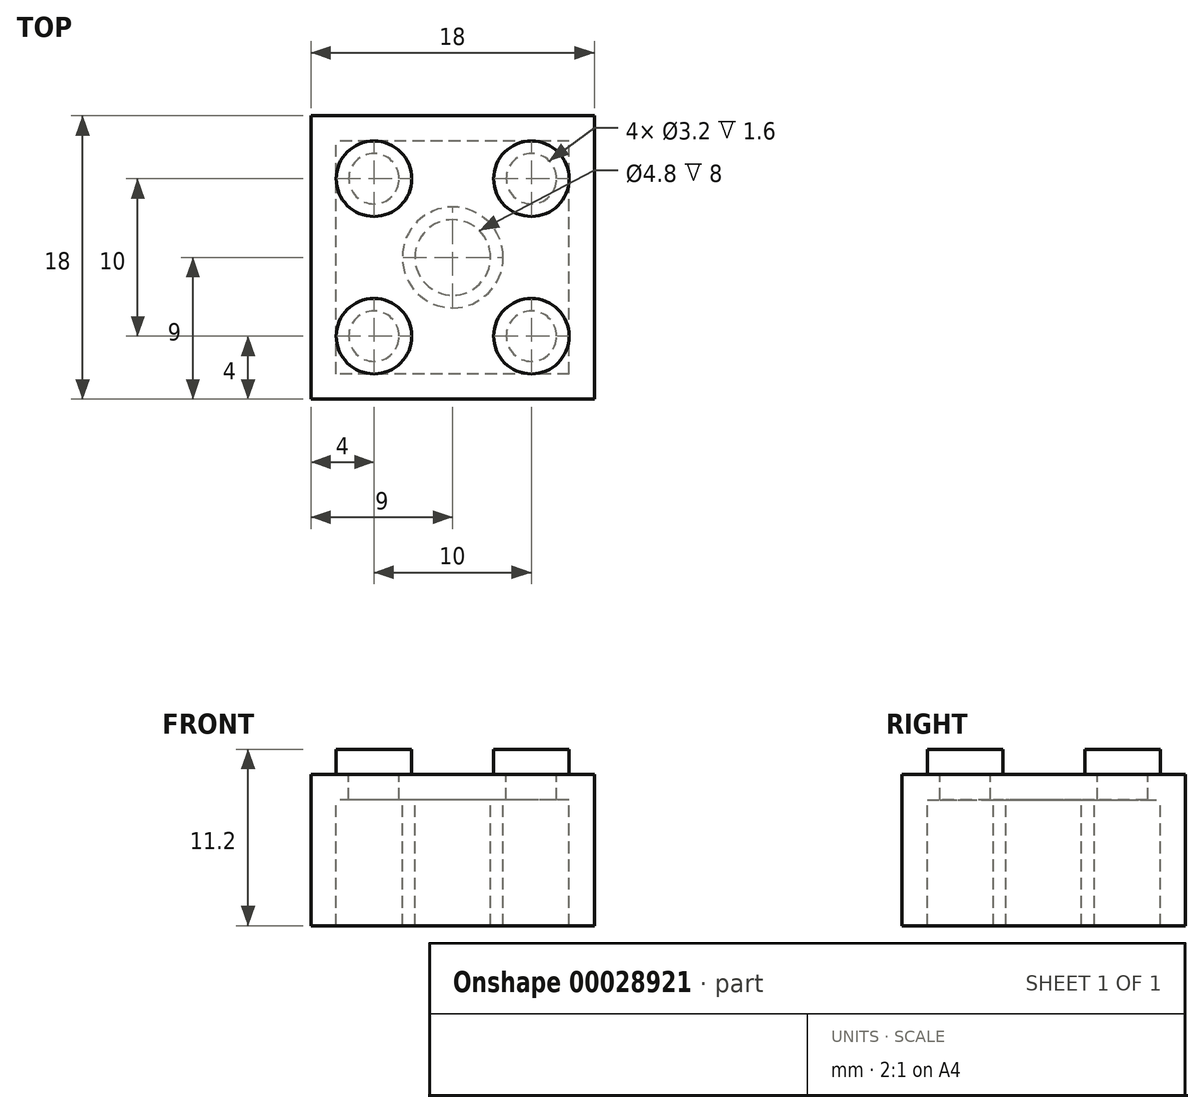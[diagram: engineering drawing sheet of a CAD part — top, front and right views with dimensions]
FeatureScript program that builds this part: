
annotation { "Feature Type Name" : "Feature", "Feature Type Description" : "" }
export const myFeature = defineFeature(function(context is Context, id is Id, definition is map)
    precondition{}
    {
        {
            var Q0;
            Q0=qCreatedBy(makeId("Top.planeOp"),FACE);
            var sketch = newSketch(context, id + "F0", { "sketchPlane" : qUnion([Q0])});
            skLineSegment(sketch, "E0.rect.bottom", {"start": v(9, -9) * mm, "end": v(-9, -9) * mm});
            skLineSegment(sketch, "E0.rect.top", {"start": v(9, 9) * mm, "end": v(-9, 9) * mm});
            skLineSegment(sketch, "E0.rect.left", {"start": v(9, -9) * mm, "end": v(9, 9) * mm});
            skLineSegment(sketch, "E0.rect.right", {"start": v(-9, -9) * mm, "end": v(-9, 9) * mm});
            skPoint(sketch, "E0.rect.middle", {"position": v(0, 0) * mm});
            skCircle(sketch, "E1", {"center": v(-5, -5) * mm, "radius": 2.4 * mm});
            skCircle(sketch, "E2", {"center": v(0, 0) * mm, "radius": 2.4 * mm});
            skCircle(sketch, "E3", {"center": v(0, 0) * mm, "radius": 3.2 * mm});
            skCircle(sketch, "E4.0.1.0", {"center": v(-5, 5) * mm, "radius": 2.4 * mm});
            skCircle(sketch, "E4.1.0.0", {"center": v(5, -5) * mm, "radius": 2.4 * mm});
            skCircle(sketch, "E4.1.1.0", {"center": v(5, 5) * mm, "radius": 2.4 * mm});
            skLineSegment(sketch, "E4.direction1", {"start": v(-5, -5) * mm, "end": v(5, -5) * mm, "construction": true});
            skLineSegment(sketch, "E4.direction2", {"start": v(-5, -5) * mm, "end": v(-5, 5) * mm, "construction": true});
            skLineSegment(sketch, "E5.0", {"start": v(7.4, 7.4) * mm, "end": v(-7.4, 7.4) * mm});
            skLineSegment(sketch, "E5.1", {"start": v(7.4, -7.4) * mm, "end": v(7.4, 7.4) * mm});
            skLineSegment(sketch, "E5.2", {"start": v(7.4, -7.4) * mm, "end": v(-7.4, -7.4) * mm});
            skLineSegment(sketch, "E5.3", {"start": v(-7.4, -7.4) * mm, "end": v(-7.4, 7.4) * mm});
            skCircle(sketch, "E6", {"center": v(-5, 5) * mm, "radius": 1.6 * mm});
            skCircle(sketch, "E7.0.1.0", {"center": v(-5, -5) * mm, "radius": 1.6 * mm});
            skCircle(sketch, "E7.1.0.0", {"center": v(5, 5) * mm, "radius": 1.6 * mm});
            skCircle(sketch, "E7.1.1.0", {"center": v(5, -5) * mm, "radius": 1.6 * mm});
            skLineSegment(sketch, "E7.direction1", {"start": v(-5, 5) * mm, "end": v(5, 5) * mm, "construction": true});
            skLineSegment(sketch, "E7.direction2", {"start": v(-5, 5) * mm, "end": v(-5, -5) * mm, "construction": true});
            skSolve(sketch);
        }
        {
            var Q0;
            {var subQ0=sQuery(id+"F0.wireOp",EDGE,"E4.0.1.0");var subQ2=makeQuery(id+"F0.imprint","INTERSECT",VERTEX,{"derivedFrom":[subQ0,sQuery(id+"F0.wireOp",EDGE,"E5.0")]});Q0=makeQuery(id+"F0.imprint","IMPRINT",FACE,{"disambiguationData":[TD([[makeQuery(id+"F0.imprint","IMPRINT",EDGE,{"disambiguationData":[TD([[subQ2,-1.0]])],"derivedFrom":subQ0}),1.0]])]});}
            var Q1;
            {var subQ0=sQuery(id+"F0.wireOp",EDGE,"E4.1.1.0");var subQ2=makeQuery(id+"F0.imprint","INTERSECT",VERTEX,{"derivedFrom":[subQ0,sQuery(id+"F0.wireOp",EDGE,"E5.0")]});Q1=makeQuery(id+"F0.imprint","IMPRINT",FACE,{"disambiguationData":[TD([[makeQuery(id+"F0.imprint","IMPRINT",EDGE,{"disambiguationData":[TD([[subQ2,1.0]])],"derivedFrom":subQ0}),1.0]])]});}
            var Q2;
            {var subQ0=sQuery(id+"F0.wireOp",EDGE,"E4.1.0.0");var subQ2=makeQuery(id+"F0.imprint","INTERSECT",VERTEX,{"derivedFrom":[subQ0,sQuery(id+"F0.wireOp",EDGE,"E5.1")]});Q2=makeQuery(id+"F0.imprint","IMPRINT",FACE,{"disambiguationData":[TD([[makeQuery(id+"F0.imprint","IMPRINT",EDGE,{"disambiguationData":[TD([[subQ2,-1.0]])],"derivedFrom":subQ0}),1.0]])]});}
            var Q3;
            {var subQ0=sQuery(id+"F0.wireOp",EDGE,"E1");var subQ2=makeQuery(id+"F0.imprint","INTERSECT",VERTEX,{"derivedFrom":[subQ0,sQuery(id+"F0.wireOp",EDGE,"E5.2")]});Q3=makeQuery(id+"F0.imprint","IMPRINT",FACE,{"disambiguationData":[TD([[makeQuery(id+"F0.imprint","IMPRINT",EDGE,{"disambiguationData":[TD([[subQ2,1.0]])],"derivedFrom":subQ0}),1.0]])]});}
            var Q4;
            Q4=makeQuery(id+"F0.imprint","IMPRINT",FACE,{"disambiguationData":[TD([[makeQuery(id+"F0.imprint","IMPRINT",EDGE,{"derivedFrom":sQuery(id+"F0.wireOp",EDGE,"E6")}),1.0]])]});
            var Q5;
            Q5=makeQuery(id+"F0.imprint","IMPRINT",FACE,{"disambiguationData":[TD([[makeQuery(id+"F0.imprint","IMPRINT",EDGE,{"derivedFrom":sQuery(id+"F0.wireOp",EDGE,"E7.0.1.0")}),1.0]])]});
            var Q6;
            Q6=makeQuery(id+"F0.imprint","IMPRINT",FACE,{"disambiguationData":[TD([[makeQuery(id+"F0.imprint","IMPRINT",EDGE,{"derivedFrom":sQuery(id+"F0.wireOp",EDGE,"E7.1.1.0")}),1.0]])]});
            var Q7;
            Q7=makeQuery(id+"F0.imprint","IMPRINT",FACE,{"disambiguationData":[TD([[makeQuery(id+"F0.imprint","IMPRINT",EDGE,{"derivedFrom":sQuery(id+"F0.wireOp",EDGE,"E7.1.0.0")}),1.0]])]});
            extrude(context, id + "F1", {"entities" : qUnion([Q0, Q1, Q2, Q3, Q4, Q5, Q6, Q7]), "depth" : 1.6 * mm});
        }
        {
            var Q0;
            Q0=makeQuery(id+"F0.imprint","IMPRINT",FACE,{"disambiguationData":[TD([[makeQuery(id+"F0.imprint","IMPRINT",EDGE,{"derivedFrom":sQuery(id+"F0.wireOp",EDGE,"E3")}),-1.0]])]});
            var Q1;
            {var subQ0=sQuery(id+"F0.wireOp",EDGE,"E5.0");var subQ1=sQuery(id+"F0.wireOp",EDGE,"E4.1.1.0");var subQ2=makeQuery(id+"F0.imprint","INTERSECT",VERTEX,{"derivedFrom":[subQ1,subQ0]});Q1=makeQuery(id+"F0.imprint","IMPRINT",FACE,{"disambiguationData":[TD([[makeQuery(id+"F0.imprint","IMPRINT",EDGE,{"disambiguationData":[TD([[subQ2,1.0]])],"derivedFrom":subQ1}),-1.0]])]});}
            var Q2;
            {var subQ1=sQuery(id+"F0.wireOp",EDGE,"E4.1.0.0");var subQ3=sQuery(id+"F0.wireOp",EDGE,"E5.1");var subQ5=makeQuery(id+"F0.imprint","INTERSECT",VERTEX,{"derivedFrom":[subQ1,subQ3]});Q2=makeQuery(id+"F0.imprint","IMPRINT",FACE,{"disambiguationData":[TD([[makeQuery(id+"F0.imprint","IMPRINT",EDGE,{"disambiguationData":[TD([[subQ5,1.0]])],"derivedFrom":subQ1}),-1.0]])]});}
            var Q3;
            {var subQ1=sQuery(id+"F0.wireOp",EDGE,"E1");var subQ3=sQuery(id+"F0.wireOp",EDGE,"E5.2");var subQ5=makeQuery(id+"F0.imprint","INTERSECT",VERTEX,{"derivedFrom":[subQ1,subQ3]});Q3=makeQuery(id+"F0.imprint","IMPRINT",FACE,{"disambiguationData":[TD([[makeQuery(id+"F0.imprint","IMPRINT",EDGE,{"disambiguationData":[TD([[subQ5,1.0]])],"derivedFrom":subQ1}),-1.0]])]});}
            var Q4;
            {var subQ1=sQuery(id+"F0.wireOp",EDGE,"E4.0.1.0");var subQ3=sQuery(id+"F0.wireOp",EDGE,"E5.0");var subQ5=makeQuery(id+"F0.imprint","INTERSECT",VERTEX,{"derivedFrom":[subQ1,subQ3]});Q4=makeQuery(id+"F0.imprint","IMPRINT",FACE,{"disambiguationData":[TD([[makeQuery(id+"F0.imprint","IMPRINT",EDGE,{"disambiguationData":[TD([[subQ5,-1.0]])],"derivedFrom":subQ1}),-1.0]])]});}
            var Q5;
            Q5=makeQuery(id+"F0.imprint","IMPRINT",FACE,{"disambiguationData":[TD([[makeQuery(id+"F0.imprint","IMPRINT",EDGE,{"derivedFrom":sQuery(id+"F0.wireOp",EDGE,"E2")}),-1.0]])]});
            var Q6;
            Q6=makeQuery(id+"F0.imprint","IMPRINT",FACE,{"disambiguationData":[TD([[makeQuery(id+"F0.imprint","IMPRINT",EDGE,{"derivedFrom":sQuery(id+"F0.wireOp",EDGE,"E2")}),1.0]])]});
            var Q7;
            Q7=makeQuery(id+"F0.imprint","IMPRINT",FACE,{"disambiguationData":[TD([[makeQuery(id+"F0.imprint","IMPRINT",EDGE,{"derivedFrom":sQuery(id+"F0.wireOp",EDGE,"E7.0.1.0")}),-1.0]])]});
            var Q8;
            Q8=makeQuery(id+"F0.imprint","IMPRINT",FACE,{"disambiguationData":[TD([[makeQuery(id+"F0.imprint","IMPRINT",EDGE,{"derivedFrom":sQuery(id+"F0.wireOp",EDGE,"E7.1.1.0")}),-1.0]])]});
            var Q9;
            Q9=makeQuery(id+"F0.imprint","IMPRINT",FACE,{"disambiguationData":[TD([[makeQuery(id+"F0.imprint","IMPRINT",EDGE,{"derivedFrom":sQuery(id+"F0.wireOp",EDGE,"E7.1.0.0")}),-1.0]])]});
            var Q10;
            Q10=makeQuery(id+"F0.imprint","IMPRINT",FACE,{"disambiguationData":[TD([[makeQuery(id+"F0.imprint","IMPRINT",EDGE,{"derivedFrom":sQuery(id+"F0.wireOp",EDGE,"E6")}),-1.0]])]});
            extrude(context, id + "F2", {"entities" : qUnion([Q0, Q1, Q2, Q3, Q4, Q5, Q6, Q7, Q8, Q9, Q10]), "operationType" : NewBodyOperationType.ADD, "oppositeDirection" : true, "depth" : 1.6 * mm});
        }
        {
            var Q0;
            Q0=makeQuery(id+"F0.imprint","IMPRINT",FACE,{"disambiguationData":[TD([[makeQuery(id+"F0.imprint","IMPRINT",EDGE,{"derivedFrom":sQuery(id+"F0.wireOp",EDGE,"E0.rect.bottom")}),-1.0]])]});
            var Q1;
            Q1=makeQuery(id+"F0.imprint","IMPRINT",FACE,{"disambiguationData":[TD([[makeQuery(id+"F0.imprint","IMPRINT",EDGE,{"derivedFrom":sQuery(id+"F0.wireOp",EDGE,"E2")}),-1.0]])]});
            extrude(context, id + "F3", {"entities" : qUnion([Q0, Q1]), "operationType" : NewBodyOperationType.ADD, "oppositeDirection" : true, "depth" : 9.6 * mm});
        }
    });
